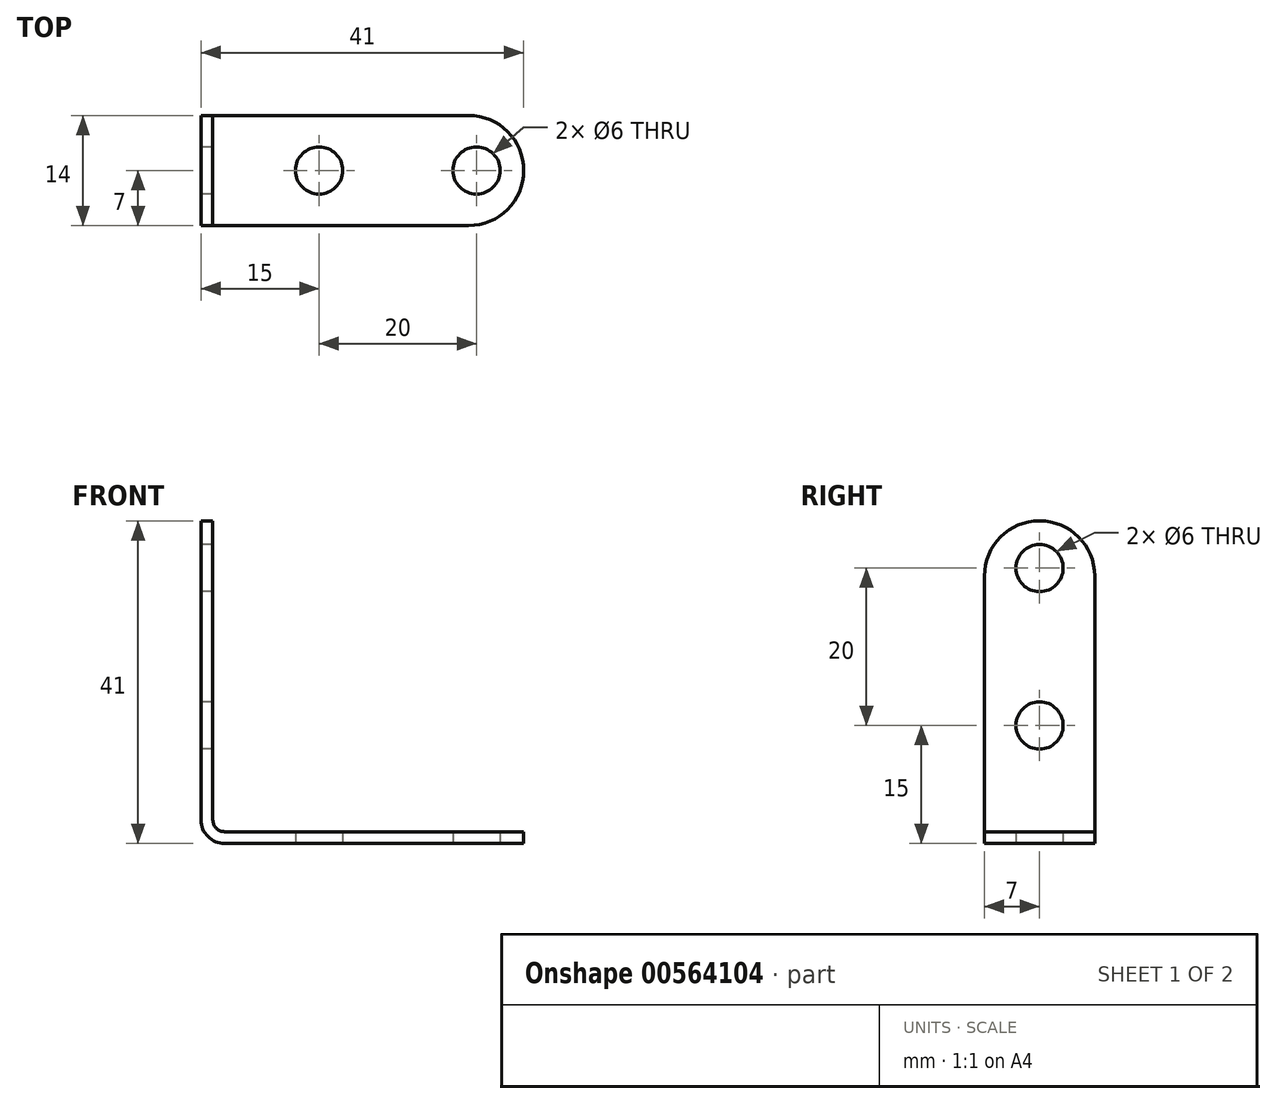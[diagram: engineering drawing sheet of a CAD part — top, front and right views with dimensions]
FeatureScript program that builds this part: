
annotation { "Feature Type Name" : "Feature", "Feature Type Description" : "" }
export const myFeature = defineFeature(function(context is Context, id is Id, definition is map)
    precondition{}
    {
        {
            var Q0;
            Q0=qCreatedBy(makeId("Front.planeOp"),FACE);
            var sketch = newSketch(context, id + "F0", { "sketchPlane" : qUnion([Q0])});
            skLineSegment(sketch, "E0", {"start": v(41, 0) * mm, "end": v(3, 0) * mm});
            skLineSegment(sketch, "E1", {"start": v(0, 3) * mm, "end": v(0, 41) * mm});
            skLineSegment(sketch, "E2", {"start": v(0, 41) * mm, "end": v(1.5, 41) * mm});
            skLineSegment(sketch, "E3", {"start": v(1.5, 41) * mm, "end": v(1.5, 3) * mm});
            skLineSegment(sketch, "E4", {"start": v(3, 1.5) * mm, "end": v(41, 1.5) * mm});
            skLineSegment(sketch, "E5", {"start": v(41, 1.5) * mm, "end": v(41, 0) * mm});
            skPoint(sketch, "E6.visualSharp", {"position": v(1.5, 1.5) * mm});
            skArc(sketch, "E6.filletArc", {"start": v(1.5, 3) * mm, "mid": v(1.94, 1.94) * mm, "end": v(3, 1.5) * mm});
            skPoint(sketch, "E7.visualSharp", {"position": v(0, 0) * mm});
            skArc(sketch, "E7.filletArc", {"start": v(0, 3) * mm, "mid": v(0.88, 0.88) * mm, "end": v(3, 0) * mm});
            skSolve(sketch);
        }
        {
            var Q0;
            Q0 = qSketchRegion(id + "F0", true);
            extrude(context, id + "F1", {"entities" : qUnion([Q0]), "depth" : 14 * mm, "offsetDistance" : 25 * mm});
        }
        {
            var Q0;
            Q0=makeQuery(id+"F1.opExtrude","CAP_EDGE",EDGE,{"disambiguationData":[OSD([sQuery(id+"F0.wireOp",EDGE,"E5")])],"isStart":true});
            var Q1;
            Q1=makeQuery(id+"F1.opExtrude","CAP_EDGE",EDGE,{"disambiguationData":[OSD([sQuery(id+"F0.wireOp",EDGE,"E5")])],"isStart":false});
            var Q2;
            Q2=makeQuery(id+"F1.opExtrude","CAP_EDGE",EDGE,{"disambiguationData":[OSD([sQuery(id+"F0.wireOp",EDGE,"E2")])],"isStart":true});
            var Q3;
            Q3=makeQuery(id+"F1.opExtrude","CAP_EDGE",EDGE,{"disambiguationData":[OSD([sQuery(id+"F0.wireOp",EDGE,"E2")])],"isStart":false});
            fillet(context, id + "F2", {"entities" : qUnion([Q0, Q1, Q2, Q3]), "radius" : 7 * mm, "tangentPropagation" : true, "allowEdgeOverflow" : false});
        }
        {
            var Q0;
            Q0=makeQuery(id+"F1.opExtrude","SWEPT_FACE",FACE,{"disambiguationData":[OSD([sQuery(id+"F0.wireOp",EDGE,"E1")])]});
            var sketch = newSketch(context, id + "F3", { "sketchPlane" : qUnion([Q0])});
            skCircle(sketch, "E8", {"center": v(7, 15) * mm, "radius": 3 * mm});
            skCircle(sketch, "E9", {"center": v(7, 35) * mm, "radius": 3 * mm});
            skSolve(sketch);
        }
        {
            var Q0;
            Q0 = qSketchRegion(id + "F3", true);
            extrude(context, id + "F4", {"entities" : qUnion([Q0]), "operationType" : NewBodyOperationType.REMOVE, "oppositeDirection" : true, "depth" : 25 * mm, "offsetDistance" : 25 * mm});
        }
        {
            var Q0;
            Q0=makeQuery(id+"F1.opExtrude","SWEPT_FACE",FACE,{"disambiguationData":[OSD([sQuery(id+"F0.wireOp",EDGE,"E0")])]});
            var sketch = newSketch(context, id + "F5", { "sketchPlane" : qUnion([Q0])});
            skCircle(sketch, "E10", {"center": v(35, 7) * mm, "radius": 3 * mm});
            skCircle(sketch, "E11", {"center": v(15, 7) * mm, "radius": 3 * mm});
            skSolve(sketch);
        }
        {
            var Q0;
            Q0 = qSketchRegion(id + "F5", true);
            extrude(context, id + "F6", {"entities" : qUnion([Q0]), "operationType" : NewBodyOperationType.REMOVE, "oppositeDirection" : true, "depth" : 25 * mm, "offsetDistance" : 25 * mm});
        }
    });
